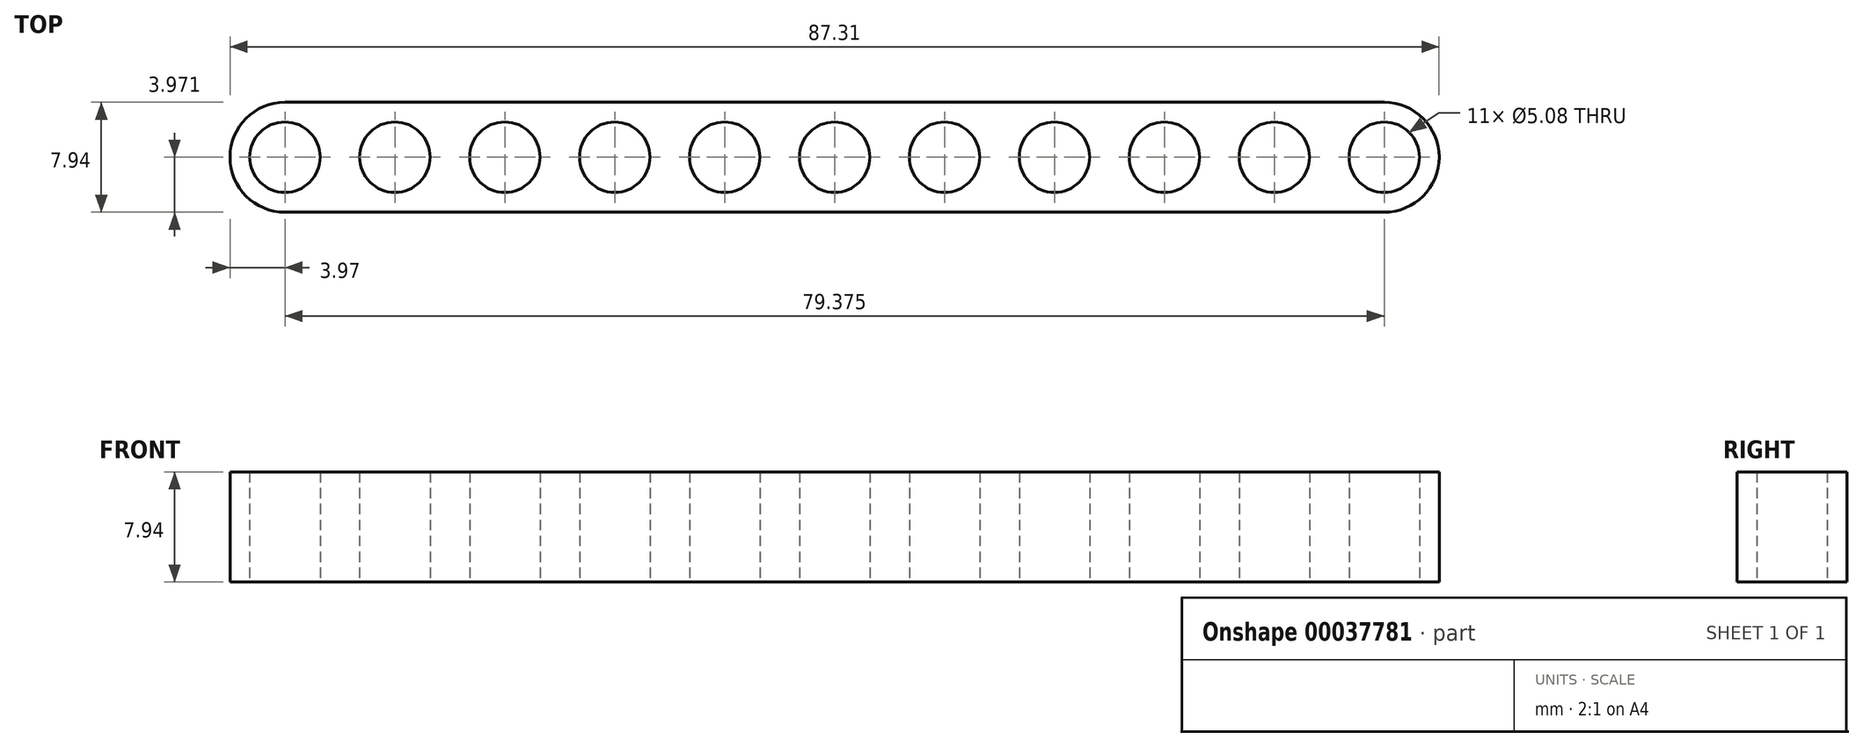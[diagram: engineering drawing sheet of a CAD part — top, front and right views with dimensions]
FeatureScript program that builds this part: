
annotation { "Feature Type Name" : "Feature", "Feature Type Description" : "" }
export const myFeature = defineFeature(function(context is Context, id is Id, definition is map)
    precondition{}
    {
        {
            var Q0;
            Q0=qCreatedBy(makeId("Top.planeOp"),FACE);
            var sketch = newSketch(context, id + "F0", { "sketchPlane" : qUnion([Q0])});
            skLineSegment(sketch, "E0.bottom", {"start": v(0, 0) * mm, "end": v(79.37, 0) * mm});
            skLineSegment(sketch, "E0.top", {"start": v(0, -7.94) * mm, "end": v(79.37, -7.94) * mm});
            skLineSegment(sketch, "E0.left", {"start": v(0, 0) * mm, "end": v(0, -7.94) * mm});
            skLineSegment(sketch, "E1", {"start": v(15.88, -3.97) * mm, "end": v(23.81, -3.97) * mm, "construction": true});
            skLineSegment(sketch, "E2", {"start": v(23.81, -3.97) * mm, "end": v(31.75, -3.97) * mm, "construction": true});
            skLineSegment(sketch, "E3", {"start": v(31.75, -3.97) * mm, "end": v(39.69, -3.97) * mm, "construction": true});
            skLineSegment(sketch, "E4", {"start": v(39.69, -3.97) * mm, "end": v(47.63, -3.97) * mm, "construction": true});
            skArc(sketch, "E5", {"start": v(0, 0) * mm, "mid": v(-3.97, -3.97) * mm, "end": v(0, -7.94) * mm});
            skCircle(sketch, "E6", {"center": v(0, -3.97) * mm, "radius": 2.54 * mm});
            skCircle(sketch, "E7", {"center": v(23.81, -3.97) * mm, "radius": 2.54 * mm});
            skCircle(sketch, "E8", {"center": v(31.75, -3.97) * mm, "radius": 2.54 * mm});
            skCircle(sketch, "E9", {"center": v(39.69, -3.97) * mm, "radius": 2.54 * mm});
            skCircle(sketch, "E10", {"center": v(47.63, -3.97) * mm, "radius": 2.54 * mm});
            skLineSegment(sketch, "E11", {"start": v(47.63, -3.97) * mm, "end": v(55.56, -3.97) * mm, "construction": true});
            skLineSegment(sketch, "E12", {"start": v(55.56, -3.97) * mm, "end": v(63.5, -3.97) * mm, "construction": true});
            skLineSegment(sketch, "E13", {"start": v(63.5, -3.97) * mm, "end": v(71.44, -3.97) * mm, "construction": true});
            skLineSegment(sketch, "E14", {"start": v(71.44, -3.97) * mm, "end": v(79.38, -3.97) * mm, "construction": true});
            skLineSegment(sketch, "E15", {"start": v(79.38, 0) * mm, "end": v(79.38, -7.94) * mm, "construction": true});
            skArc(sketch, "E16", {"start": v(79.37, -7.94) * mm, "mid": v(83.34, -3.97) * mm, "end": v(79.37, 0) * mm});
            skCircle(sketch, "E17", {"center": v(55.56, -3.97) * mm, "radius": 2.54 * mm});
            skCircle(sketch, "E18", {"center": v(63.5, -3.97) * mm, "radius": 2.54 * mm});
            skCircle(sketch, "E19", {"center": v(71.44, -3.97) * mm, "radius": 2.54 * mm});
            skCircle(sketch, "E20", {"center": v(79.38, -3.97) * mm, "radius": 2.54 * mm});
            skLineSegment(sketch, "E21", {"start": v(0, -3.97) * mm, "end": v(7.94, -3.97) * mm, "construction": true});
            skLineSegment(sketch, "E22", {"start": v(7.94, -3.97) * mm, "end": v(15.88, -3.97) * mm, "construction": true});
            skCircle(sketch, "E23", {"center": v(7.94, -3.97) * mm, "radius": 2.54 * mm});
            skCircle(sketch, "E24", {"center": v(15.88, -3.97) * mm, "radius": 2.54 * mm});
            skSolve(sketch);
        }
        {
            var Q0;
            Q0=qSketchRegion(id+"F0",true);
            extrude(context, id + "F1", {"entities" : qUnion([Q0]), "depth" : 7.94 * mm});
        }
    });
